FCSTD DOCUMENT  (FreeCAD 0.22R35485 (Git))
Label: slideFence
License: All rights reserved
LicenseURL: http://en.wikipedia.org/wiki/All_rights_reserved
objects: Sketcher::SketchObject×1
note: 1 computed .brp shape members not serialized (recipe doc carries the construction recipe); baked Part::Feature solids carry a one-line shape summary decoded from their .brp

FEATURE [Sketcher::SketchObject] Sketch
  FullyConstrained = true
  Placement = pos=(0,0,0) rot=(1,0,0;1.5708rad)
  sketch-geometry (20):
    g0: LineSegment StartX=0 StartY=0 StartZ=0 EndX=300 EndY=700 EndZ=0
    g1: LineSegment StartX=300 StartY=700 StartZ=0 EndX=600 EndY=0 EndZ=0
    g2: LineSegment StartX=600 StartY=0 StartZ=0 EndX=900 EndY=700 EndZ=0
    g3: LineSegment StartX=900 StartY=700 StartZ=0 EndX=1200 EndY=0 EndZ=0
    g4: LineSegment StartX=1200 StartY=0 StartZ=0 EndX=1500 EndY=700 EndZ=0
    g5: LineSegment StartX=1500 StartY=700 StartZ=0 EndX=1800 EndY=0 EndZ=0
    g6: LineSegment StartX=1800 StartY=0 StartZ=0 EndX=2100 EndY=700 EndZ=0
    g7: LineSegment StartX=2100 StartY=700 StartZ=0 EndX=2400 EndY=0 EndZ=0
    g8: LineSegment StartX=2400 StartY=0 StartZ=0 EndX=2700 EndY=700 EndZ=0
    g9: LineSegment StartX=2700 StartY=700 StartZ=0 EndX=3000 EndY=0 EndZ=0
    g10: LineSegment StartX=0 StartY=700 StartZ=0 EndX=300 EndY=1.137e-13 EndZ=0
    g11: LineSegment StartX=300 StartY=1.137e-13 StartZ=0 EndX=600 EndY=700 EndZ=0
    g12: LineSegment StartX=600 StartY=700 StartZ=0 EndX=900 EndY=0 EndZ=0
    g13: LineSegment StartX=900 StartY=0 StartZ=0 EndX=1200 EndY=700 EndZ=0
    g14: LineSegment StartX=1200 StartY=700 StartZ=0 EndX=1500 EndY=0 EndZ=0
    g15: LineSegment StartX=1500 StartY=0 StartZ=0 EndX=1800 EndY=700 EndZ=0
    g16: LineSegment StartX=1800 StartY=700 StartZ=0 EndX=2100 EndY=0 EndZ=0
    g17: LineSegment StartX=2100 StartY=0 StartZ=0 EndX=2400 EndY=700 EndZ=0
    g18: LineSegment StartX=2400 StartY=700 StartZ=0 EndX=2700 EndY=0 EndZ=0
    g19: LineSegment StartX=2700 StartY=0 StartZ=0 EndX=3000 EndY=700 EndZ=0
  constraints (61):
    c: Coincident(g-1,g0)
    c: Coincident(g0,g1)
    c: PointOnObject(g1,g-1)
    c: Coincident(g1,g2)
    c: Coincident(g2,g3)
    c: PointOnObject(g3,g-1)
    c: Coincident(g3,g4)
    c: Coincident(g4,g5)
    c: Coincident(g5,g6)
    c: Coincident(g6,g7)
    c: Coincident(g7,g8)
    c: Coincident(g8,g9)
    c: PointOnObject(g9,g-1)
    c: Parallel(g0,g2)
    c: Parallel(g2,g4)
    c: Parallel(g4,g6)
    c: Parallel(g6,g8)
    c: Parallel(g1,g3)
    c: Parallel(g3,g5)
    c: Parallel(g5,g7)
    c: Equal(g0,g1)
    c: Parallel(g7,g9)
    c: Equal(g0,g2)
    c: Equal(g2,g4)
    c: Equal(g4,g6)
    c: Equal(g6,g8)
    c: PointOnObject(g7,g-1)
    c: PointOnObject(g5,g-1)
    c: PointOnObject(g10,g-2)
    c: Coincident(g10,g11)
    c: Coincident(g11,g12)
    c: PointOnObject(g12,g-1)
    c: Coincident(g12,g13)
    c: Coincident(g13,g14)
    c: Coincident(g14,g15)
    c: Coincident(g15,g16)
    c: PointOnObject(g16,g-1)
    c: Coincident(g16,g17)
    c: Coincident(g17,g18)
    c: Coincident(g18,g19)
    c: Equal(g10,g0)
    c: Equal(g10,g11)
    c: Equal(g2,g13)
    c: Equal(g4,g15)
    c: Equal(g6,g17)
    c: Equal(g8,g19)
    c: Equal(g10,g12)
    c: Equal(g3,g14)
    c: Equal(g5,g16)
    c: Equal(g7,g18)
    c: Vertical(g9,g19)
    c: PointOnObject(g18,g-1)
    c: PointOnObject(g14,g-1)
    c: Parallel(g19,g8)
    c: Parallel(g9,g18)
    c: Parallel(g10,g1)
    c: Parallel(g1,g12)
    c: Parallel(g3,g14)
    c: Parallel(g5,g16)
    c: DistanceX(g10,g19) = 3000
    c: DistanceY(g9,g19) = 700
